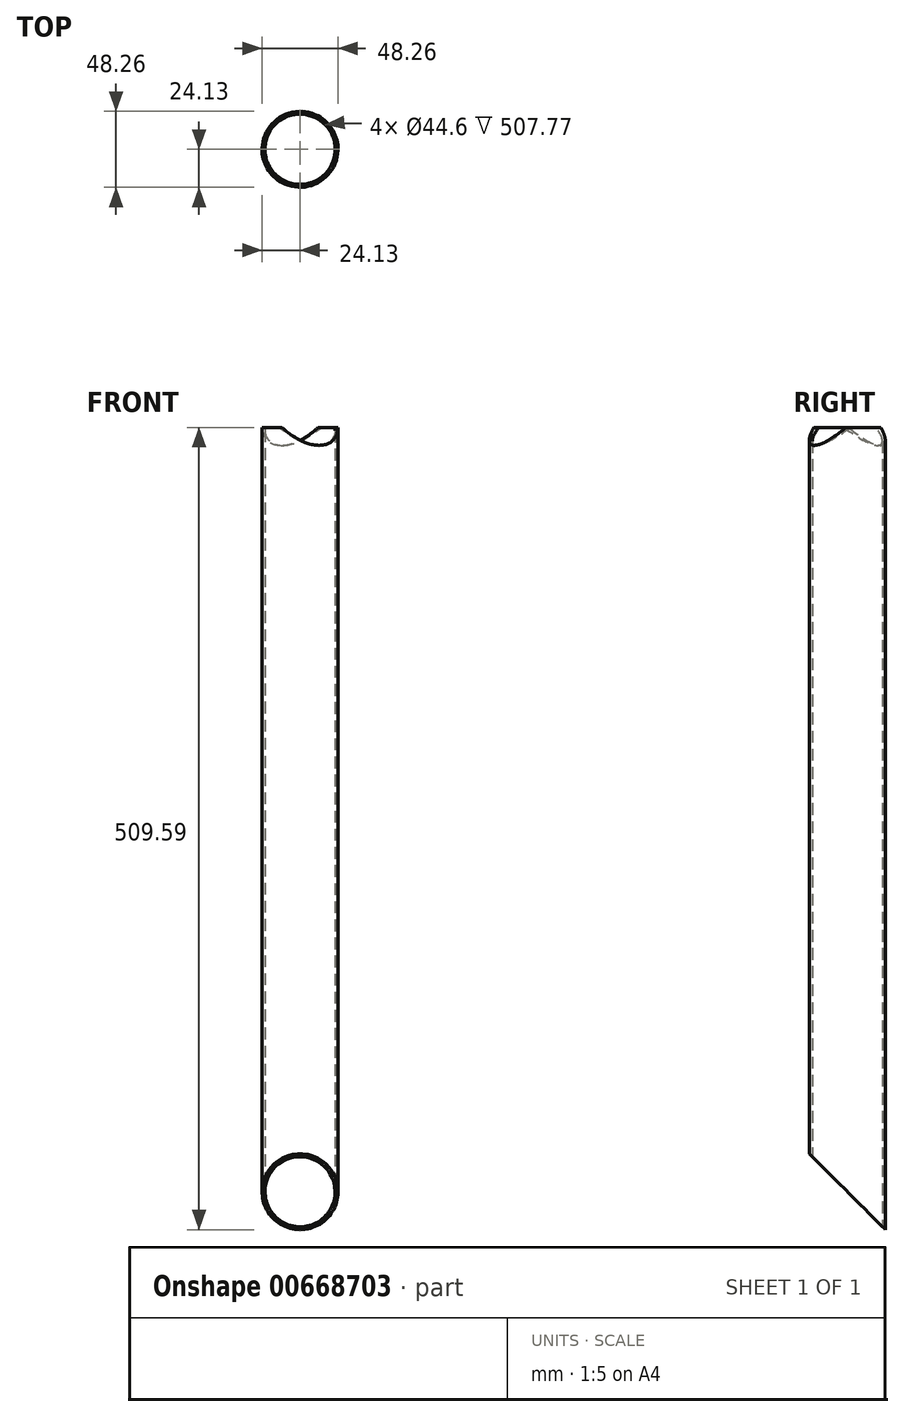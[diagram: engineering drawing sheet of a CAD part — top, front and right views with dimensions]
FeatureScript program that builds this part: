
annotation { "Feature Type Name" : "Feature", "Feature Type Description" : "" }
export const myFeature = defineFeature(function(context is Context, id is Id, definition is map)
    precondition{}
    {
        {
            var Q0;
            Q0=qCreatedBy(makeId("Top.planeOp"),FACE);
            var sketch = newSketch(context, id + "F0", { "sketchPlane" : qUnion([Q0])});
            skCircle(sketch, "E0", {"center": v(0, 0) * mm, "radius": 24.13 * mm});
            skCircle(sketch, "E1.0", {"center": v(0, 0) * mm, "radius": 22.3 * mm});
            skSolve(sketch);
        }
        {
            var Q0;
            Q0 = qSketchRegion(id + "F0", true);
            extrude(context, id + "F1", {"entities" : qUnion([Q0]), "depth" : 509.59 * mm, "offsetDistance" : 25.4 * mm});
        }
        {
            var Q0;
            Q0=qCreatedBy(makeId("Right.planeOp"),FACE);
            var sketch = newSketch(context, id + "F2", { "sketchPlane" : qUnion([Q0])});
            skLineSegment(sketch, "E2.bottom", {"start": v(-24.13, 0) * mm, "end": v(24.13, 0) * mm});
            skLineSegment(sketch, "E2.left", {"start": v(-24.13, 0) * mm, "end": v(-24.13, 48.26) * mm});
            skLineSegment(sketch, "E3", {"start": v(-24.13, 48.26) * mm, "end": v(24.13, 0) * mm});
            skSolve(sketch);
        }
        {
            var Q0;
            Q0 = qSketchRegion(id + "F2", true);
            extrude(context, id + "F3", {"entities" : qUnion([Q0]), "operationType" : NewBodyOperationType.REMOVE, "endBound" : BoundingType.THROUGH_ALL, "oppositeDirection" : true, "depth" : 25.4 * mm, "offsetDistance" : 25.4 * mm, "hasSecondDirection" : true, "secondDirectionBound" : SecondDirectionBoundingType.THROUGH_ALL, "secondDirectionOppositeDirection" : false, "secondDirectionDepth" : 25.4 * mm});
        }
        {
            var Q0;
            Q0=makeQuery(id+"F1.opExtrude","CAP_FACE",FACE,{"disambiguationData":[OSD([sQuery(id+"F0.wireOp",EDGE,"E0"),sQuery(id+"F0.wireOp",EDGE,"E1.0")])],"isStart":false});
            var sketch = newSketch(context, id + "F4", { "sketchPlane" : qUnion([Q0])});
            skLineSegment(sketch, "E4", {"start": v(-12.07, 20.9) * mm, "end": v(12.07, -20.9) * mm});
            skSolve(sketch);
        }
        {
            var Q0;
            Q0=sQuery(id+"F4.wireOp",EDGE,"E4");
            cPlane(context, id + "F5", {"entities" : qUnion([Q0]), "cplaneType" : CPlaneType.MID_PLANE, "offset" : 25.4 * mm, "width" : 152.4 * mm, "height" : 152.4 * mm});
        }
        {
            var Q0;
            Q0=qCreatedBy(id+"F5.planeOp",FACE);
            var sketch = newSketch(context, id + "F6", { "sketchPlane" : qUnion([Q0])});
            skCircle(sketch, "E5", {"center": v(0, 522.29) * mm, "radius": 24.13 * mm});
            skPoint(sketch, "E6", {"position": v(0, 509.59) * mm});
            skSolve(sketch);
        }
        {
            var Q0;
            Q0 = qSketchRegion(id + "F6", true);
            extrude(context, id + "F7", {"entities" : qUnion([Q0]), "operationType" : NewBodyOperationType.REMOVE, "oppositeDirection" : true, "depth" : 50.8 * mm, "offsetDistance" : 25.4 * mm, "hasSecondDirection" : true, "secondDirectionOppositeDirection" : false, "secondDirectionDepth" : 50.8 * mm});
        }
    });
